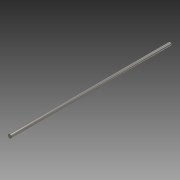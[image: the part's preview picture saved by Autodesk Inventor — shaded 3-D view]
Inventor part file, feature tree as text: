
AUTODESK INVENTOR PART (.ipt)
format: ipt  version: 2018 (Build 220112000, 112)  size: 75,264 bytes
history: native  units: mm
features: extrude x1, chamfer x1, sketch x1
ambient origin geometry x8: Origin, YZ Plane, XZ Plane, XY Plane, X Axis, Y Axis, Z Axis, Center Point
bodies: Solid1 (feature_tree)
feature tree (3):
  extrude  "Extrusion1"  Depth=500.0mm TaperAngle=0.0deg
  chamfer  "Chamfer1"  Distance=0.5mm Angle=45.0deg
  sketch  "Sketch1"  dims[d0=10.0mm d1=500.0mm d2=0.0mm d3=0.5mm d4=2.0mm d5=45.0deg]
